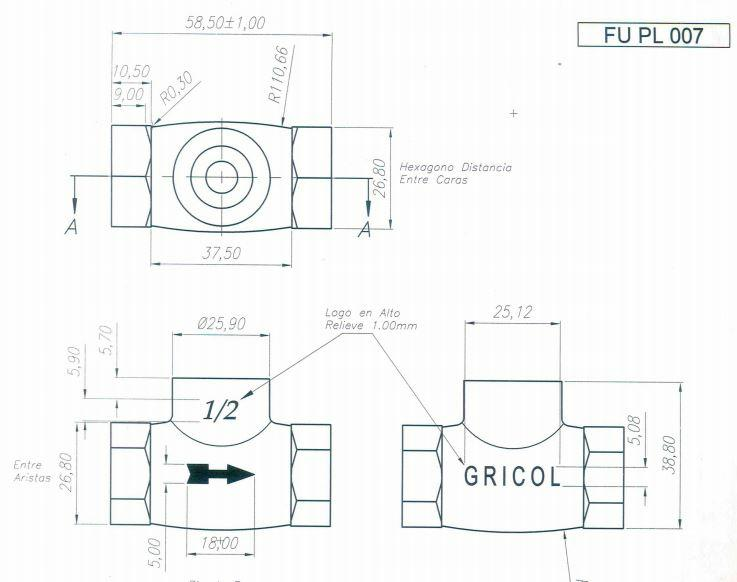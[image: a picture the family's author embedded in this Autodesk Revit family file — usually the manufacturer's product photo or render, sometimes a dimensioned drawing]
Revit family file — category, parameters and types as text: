
# Revit family: 01-0934-11 CONJUNTO REGISTRO DUCHA HELVETIA
name_source: partatom
category: Plumbing Fixtures
revit_build: Autodesk Revit 2018 (Build: 20170223_1515(x64)
units: mm (PartAtom-declared; Revit-internal decimal feet)

## family parameters
Cut with Voids When Loaded = No
Host = Face
OmniClass Number = 23.31.11.00
Part Type = Normal
Room Calculation Point = No
Round Connector Dimension = Use Diameter
Shared = No

## types (1)
- 01-0934-11
    Ancho escudo = 60 mm  [stored 0.19685 ft]
    CW Connection = Yes
    Default Elevation = 0 mm  [stored 0 ft]
    Description = Mezclador ducha
    HW Connection = Yes
    Laton = Laton
    Link Ficha Tecnica = No encontrada en internet
    Manija = 70 mm  [stored 0.229659 ft]
    Manufacturer = Gricol
    Model = 01-0934-11
    Plastico - ABS Cromado = Plastico - ABS Cromado
    Product Name = CONJUNTO REGISTRO DUCHA HELVETIA
    Type Image = LOGO-01.jpg
    URL = https://www.gricol.com
    Vent Connection = No
    Waste Connection = No

note: [stored X ft] marks values corroborated as IEEE doubles in the binary element streams (Revit-internal decimal feet)

## geometry (parser evidence)
native form markers: Blend x4, Sweep x21
no freeform markers — native parametric forms only
